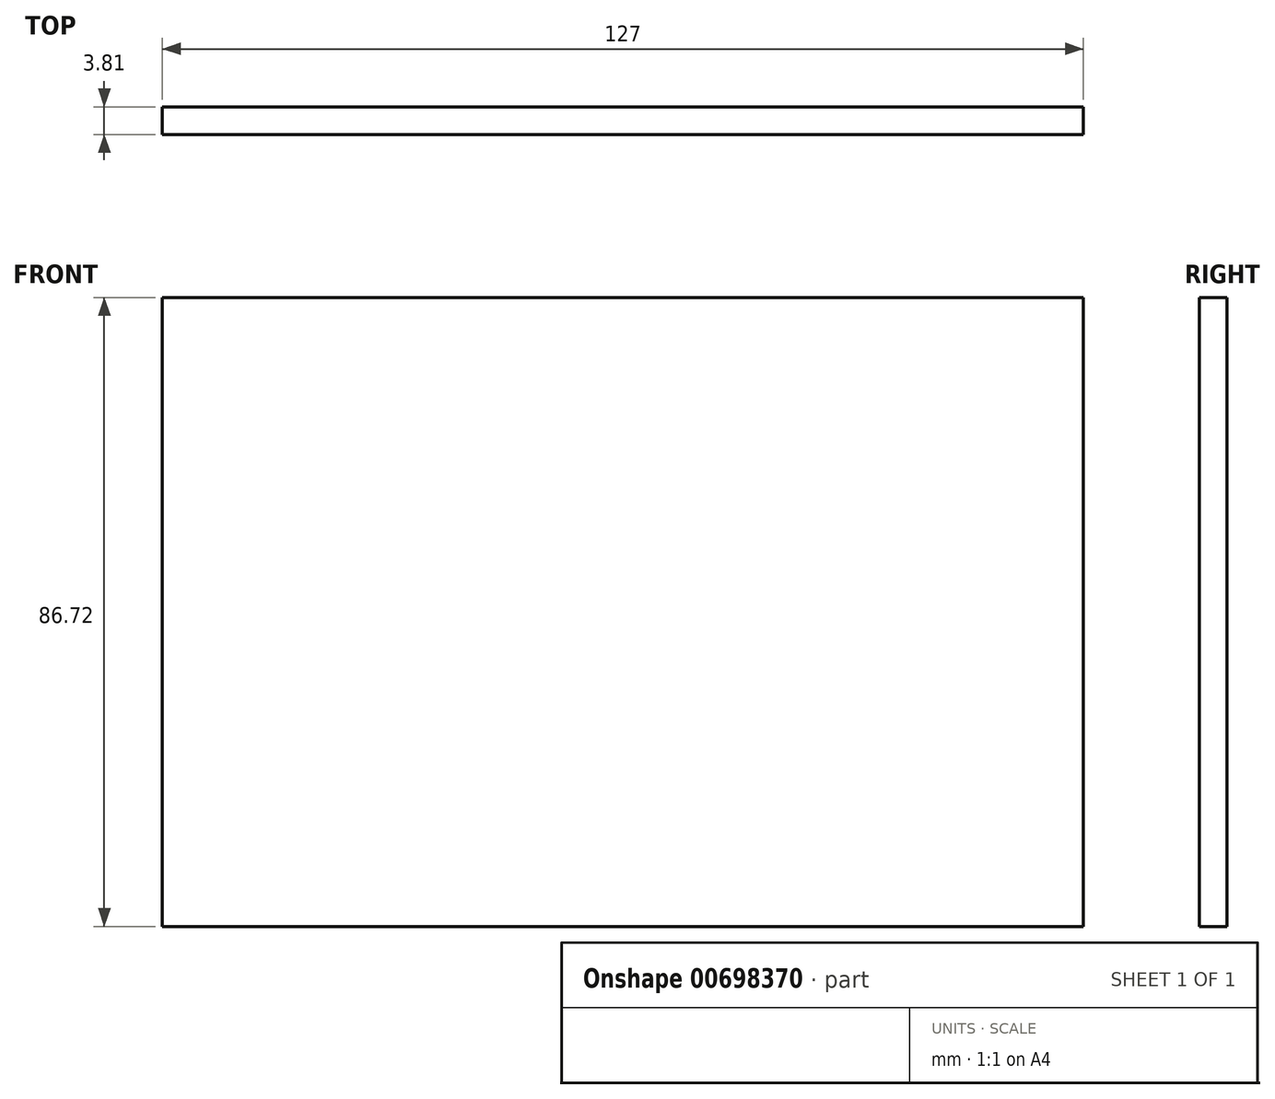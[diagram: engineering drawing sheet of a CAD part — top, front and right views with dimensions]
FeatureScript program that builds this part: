
annotation { "Feature Type Name" : "Feature", "Feature Type Description" : "" }
export const myFeature = defineFeature(function(context is Context, id is Id, definition is map)
    precondition{}
    {
        {
            var Q0;
            Q0=qCreatedBy(makeId("Front.planeOp"),FACE);
            var sketch = newSketch(context, id + "F0", { "sketchPlane" : qUnion([Q0])});
            skLineSegment(sketch, "E0.bottom", {"start": v(-63.5, 43.36) * mm, "end": v(63.5, 43.36) * mm});
            skLineSegment(sketch, "E0.top", {"start": v(-63.5, -43.36) * mm, "end": v(63.5, -43.36) * mm});
            skLineSegment(sketch, "E0.left", {"start": v(-63.5, 43.36) * mm, "end": v(-63.5, -43.36) * mm});
            skLineSegment(sketch, "E0.right", {"start": v(63.5, 43.36) * mm, "end": v(63.5, -43.36) * mm});
            skPoint(sketch, "E0.middle", {"position": v(0, 0) * mm});
            skSolve(sketch);
        }
        {
            var Q0;
            Q0 = qSketchRegion(id + "F0", true);
            extrude(context, id + "F1", {"entities" : qUnion([Q0]), "depth" : 3.8 * mm, "offsetDistance" : 25.4 * mm});
        }
    });
